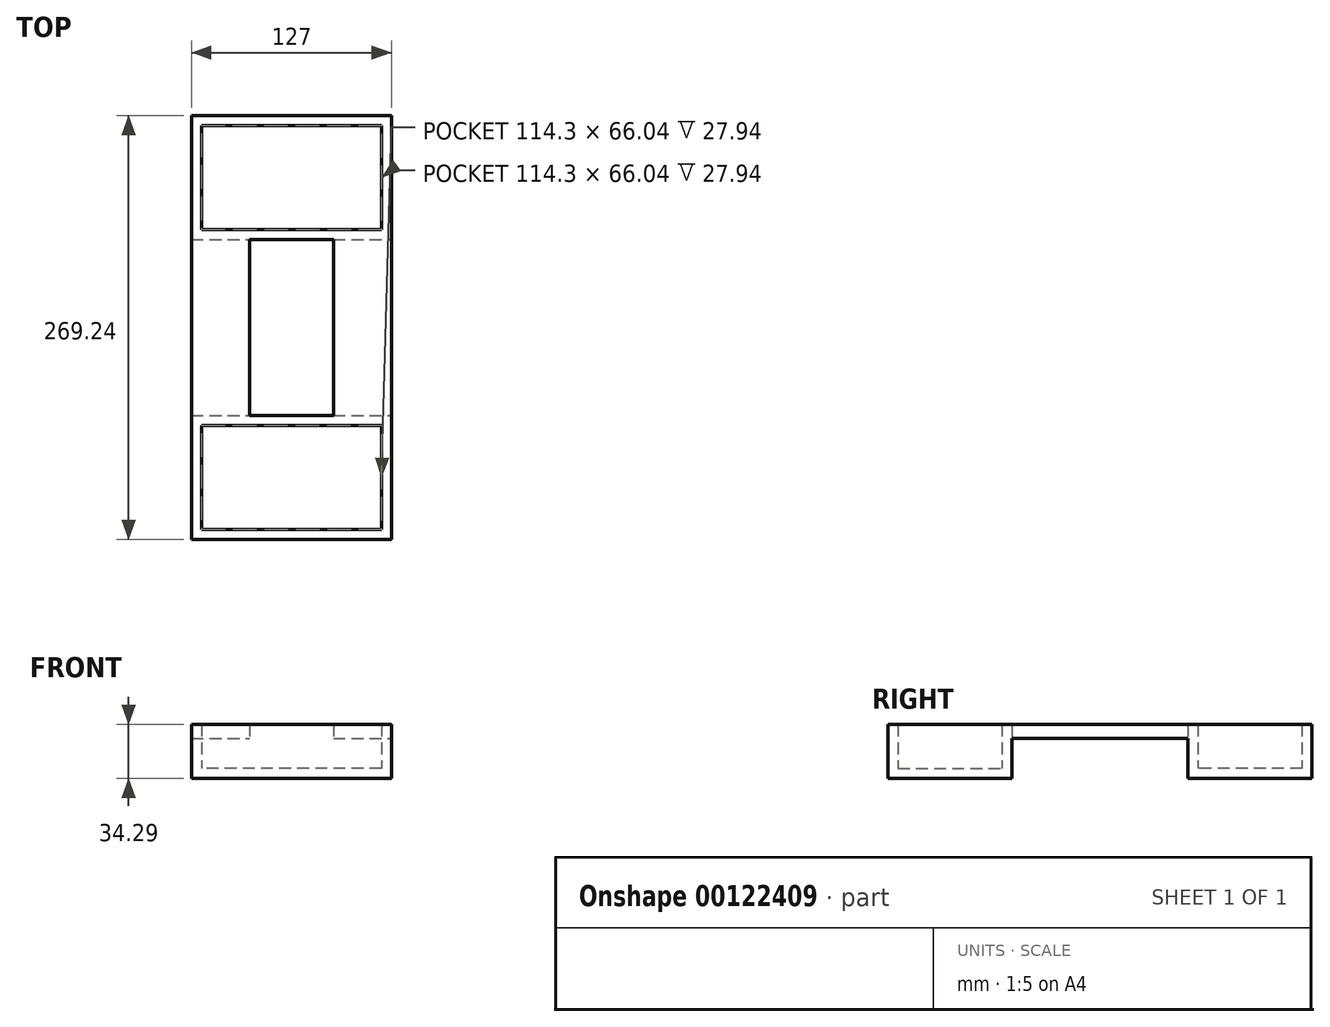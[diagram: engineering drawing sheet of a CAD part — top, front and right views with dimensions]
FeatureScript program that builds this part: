
annotation { "Feature Type Name" : "Feature", "Feature Type Description" : "" }
export const myFeature = defineFeature(function(context is Context, id is Id, definition is map)
    precondition{}
    {
        {
            var Q0;
            Q0=qCreatedBy(makeId("Top.planeOp"),FACE);
            var sketch = newSketch(context, id + "F0", { "sketchPlane" : qUnion([Q0])});
            skLineSegment(sketch, "E0.bottom", {"start": v(57.15, -128.27) * mm, "end": v(-57.15, -128.27) * mm});
            skLineSegment(sketch, "E0.top", {"start": v(57.15, -62.23) * mm, "end": v(-57.15, -62.23) * mm});
            skLineSegment(sketch, "E0.left", {"start": v(57.15, -128.27) * mm, "end": v(57.15, -62.23) * mm});
            skLineSegment(sketch, "E0.right", {"start": v(-57.15, -128.27) * mm, "end": v(-57.15, -62.23) * mm});
            skPoint(sketch, "E0.middle", {"position": v(0, -95.25) * mm});
            skLineSegment(sketch, "E1", {"start": v(0, -95.25) * mm, "end": v(0, 0) * mm, "construction": true});
            skLineSegment(sketch, "E2.0", {"start": v(26.67, -55.88) * mm, "end": v(-26.67, -55.88) * mm});
            skLineSegment(sketch, "E2.1", {"start": v(63.5, -134.62) * mm, "end": v(63.5, -55.88) * mm});
            skLineSegment(sketch, "E2.2", {"start": v(63.5, -134.62) * mm, "end": v(-63.5, -134.62) * mm});
            skLineSegment(sketch, "E2.3", {"start": v(-63.5, -134.62) * mm, "end": v(-63.5, -55.88) * mm});
            skLineSegment(sketch, "E3", {"start": v(-63.5, -55.88) * mm, "end": v(-63.5, 0) * mm});
            skLineSegment(sketch, "E4", {"start": v(-63.5, 0) * mm, "end": v(-26.67, 0) * mm});
            skLineSegment(sketch, "E5", {"start": v(63.5, 0) * mm, "end": v(63.5, -55.88) * mm});
            skLineSegment(sketch, "E6", {"start": v(-26.67, -55.88) * mm, "end": v(-26.67, 0) * mm});
            skLineSegment(sketch, "E7", {"start": v(26.67, -55.88) * mm, "end": v(26.67, 0) * mm});
            skLineSegment(sketch, "E8.trimOffspring", {"start": v(26.67, 0) * mm, "end": v(63.5, 0) * mm});
            skSolve(sketch);
        }
        {
            var Q0;
            Q0=qCreatedBy(makeId("Top.planeOp"),FACE);
            var sketch = newSketch(context, id + "F1", { "sketchPlane" : qUnion([Q0])});
            skLineSegment(sketch, "E9.0", {"start": v(-63.5, -55.88) * mm, "end": v(-63.5, 0) * mm});
            skLineSegment(sketch, "E10.0", {"start": v(-63.5, -134.62) * mm, "end": v(-63.5, -55.88) * mm});
            skLineSegment(sketch, "E11.0", {"start": v(63.5, -134.62) * mm, "end": v(-63.5, -134.62) * mm});
            skLineSegment(sketch, "E12.0", {"start": v(63.5, -134.62) * mm, "end": v(63.5, -55.88) * mm});
            skLineSegment(sketch, "E13.0", {"start": v(63.5, 0) * mm, "end": v(63.5, -55.88) * mm});
            skLineSegment(sketch, "E14.0", {"start": v(26.67, 0) * mm, "end": v(63.5, 0) * mm});
            skLineSegment(sketch, "E15.0", {"start": v(26.67, -55.88) * mm, "end": v(26.67, 0) * mm});
            skLineSegment(sketch, "E16.0", {"start": v(26.67, -55.88) * mm, "end": v(-26.67, -55.88) * mm});
            skLineSegment(sketch, "E17.0", {"start": v(-26.67, -55.88) * mm, "end": v(-26.67, 0) * mm});
            skLineSegment(sketch, "E18.0", {"start": v(-63.5, 0) * mm, "end": v(-26.67, 0) * mm});
            skLineSegment(sketch, "E19.0", {"start": v(57.15, -128.27) * mm, "end": v(-57.15, -128.27) * mm});
            skLineSegment(sketch, "E20.0", {"start": v(-57.15, -128.27) * mm, "end": v(-57.15, -62.23) * mm});
            skLineSegment(sketch, "E21.0", {"start": v(57.15, -62.23) * mm, "end": v(-57.15, -62.23) * mm});
            skLineSegment(sketch, "E22.0", {"start": v(57.15, -128.27) * mm, "end": v(57.15, -62.23) * mm});
            skSolve(sketch);
        }
        {
            var Q0;
            Q0 = qSketchRegion(id + "F1", true);
            extrude(context, id + "F2", {"entities" : qUnion([Q0]), "depth" : 8.9 * mm, "offsetDistance" : 25.4 * mm});
        }
        {
            var Q0;
            Q0=qCreatedBy(makeId("Top.planeOp"),FACE);
            var sketch = newSketch(context, id + "F3", { "sketchPlane" : qUnion([Q0])});
            skLineSegment(sketch, "E23.0", {"start": v(-63.5, -134.62) * mm, "end": v(-63.5, -55.88) * mm});
            skLineSegment(sketch, "E24.0", {"start": v(63.5, -134.62) * mm, "end": v(63.5, -55.88) * mm});
            skLineSegment(sketch, "E25.0", {"start": v(63.5, -134.62) * mm, "end": v(-63.5, -134.62) * mm});
            skLineSegment(sketch, "E26", {"start": v(-63.5, -55.88) * mm, "end": v(63.5, -55.88) * mm});
            skLineSegment(sketch, "E27.0", {"start": v(-57.15, -128.27) * mm, "end": v(-57.15, -62.23) * mm});
            skLineSegment(sketch, "E28.0", {"start": v(57.15, -62.23) * mm, "end": v(-57.15, -62.23) * mm});
            skLineSegment(sketch, "E29.0", {"start": v(57.15, -128.27) * mm, "end": v(57.15, -62.23) * mm});
            skLineSegment(sketch, "E30.0", {"start": v(57.15, -128.27) * mm, "end": v(-57.15, -128.27) * mm});
            skSolve(sketch);
        }
        {
            var Q0;
            Q0 = qSketchRegion(id + "F3", true);
            extrude(context, id + "F4", {"entities" : qUnion([Q0]), "operationType" : NewBodyOperationType.ADD, "oppositeDirection" : true, "depth" : 19.05 * mm, "offsetDistance" : 25.4 * mm});
        }
        {
            var Q0;
            Q0=makeQuery(id+"F4.opExtrude","CAP_FACE",FACE,{"disambiguationData":[OSD([sQuery(id+"F3.wireOp",EDGE,"E23.0"),sQuery(id+"F3.wireOp",EDGE,"E24.0"),sQuery(id+"F3.wireOp",EDGE,"E25.0"),sQuery(id+"F3.wireOp",EDGE,"E26"),sQuery(id+"F3.wireOp",EDGE,"E27.0"),sQuery(id+"F3.wireOp",EDGE,"E28.0"),sQuery(id+"F3.wireOp",EDGE,"E29.0"),sQuery(id+"F3.wireOp",EDGE,"E30.0")])],"isStart":false});
            var sketch = newSketch(context, id + "F5", { "sketchPlane" : qUnion([Q0])});
            skLineSegment(sketch, "E31.0", {"start": v(63.5, 134.62) * mm, "end": v(63.5, 55.88) * mm});
            skLineSegment(sketch, "E32.0", {"start": v(63.5, 134.62) * mm, "end": v(-63.5, 134.62) * mm});
            skLineSegment(sketch, "E33.0", {"start": v(-63.5, 55.88) * mm, "end": v(63.5, 55.88) * mm});
            skPoint(sketch, "E34.0", {"position": v(-63.5, 95.25) * mm});
            skLineSegment(sketch, "E35.0", {"start": v(-63.5, 134.62) * mm, "end": v(-63.5, 55.88) * mm});
            skSolve(sketch);
        }
        {
            var Q0;
            Q0 = qSketchRegion(id + "F5", true);
            extrude(context, id + "F6", {"entities" : qUnion([Q0]), "operationType" : NewBodyOperationType.ADD, "depth" : 6.35 * mm, "offsetDistance" : 25.4 * mm});
        }
        {
            var Q0;
            Q0=makeQuery(id+"F2.opExtrude","SWEPT_BODY",BODY,{"disambiguationData":[OSD([sQuery(id+"F1.wireOp",EDGE,"E9.0"),sQuery(id+"F1.wireOp",EDGE,"E10.0"),sQuery(id+"F1.wireOp",EDGE,"E11.0"),sQuery(id+"F1.wireOp",EDGE,"E12.0"),sQuery(id+"F1.wireOp",EDGE,"E13.0"),sQuery(id+"F1.wireOp",EDGE,"E14.0"),sQuery(id+"F1.wireOp",EDGE,"E15.0"),sQuery(id+"F1.wireOp",EDGE,"E16.0"),sQuery(id+"F1.wireOp",EDGE,"E17.0"),sQuery(id+"F1.wireOp",EDGE,"E18.0"),sQuery(id+"F1.wireOp",EDGE,"E19.0"),sQuery(id+"F1.wireOp",EDGE,"E20.0"),sQuery(id+"F1.wireOp",EDGE,"E21.0"),sQuery(id+"F1.wireOp",EDGE,"E22.0")])]});
            var Q1;
            Q1=qCreatedBy(makeId("Front.planeOp"),FACE);
            mirror(context, id + "F7", {"operationType" : NewBodyOperationType.ADD, "entities" : qUnion([Q0]), "mirrorPlane" : qUnion([Q1])});
        }
    });
